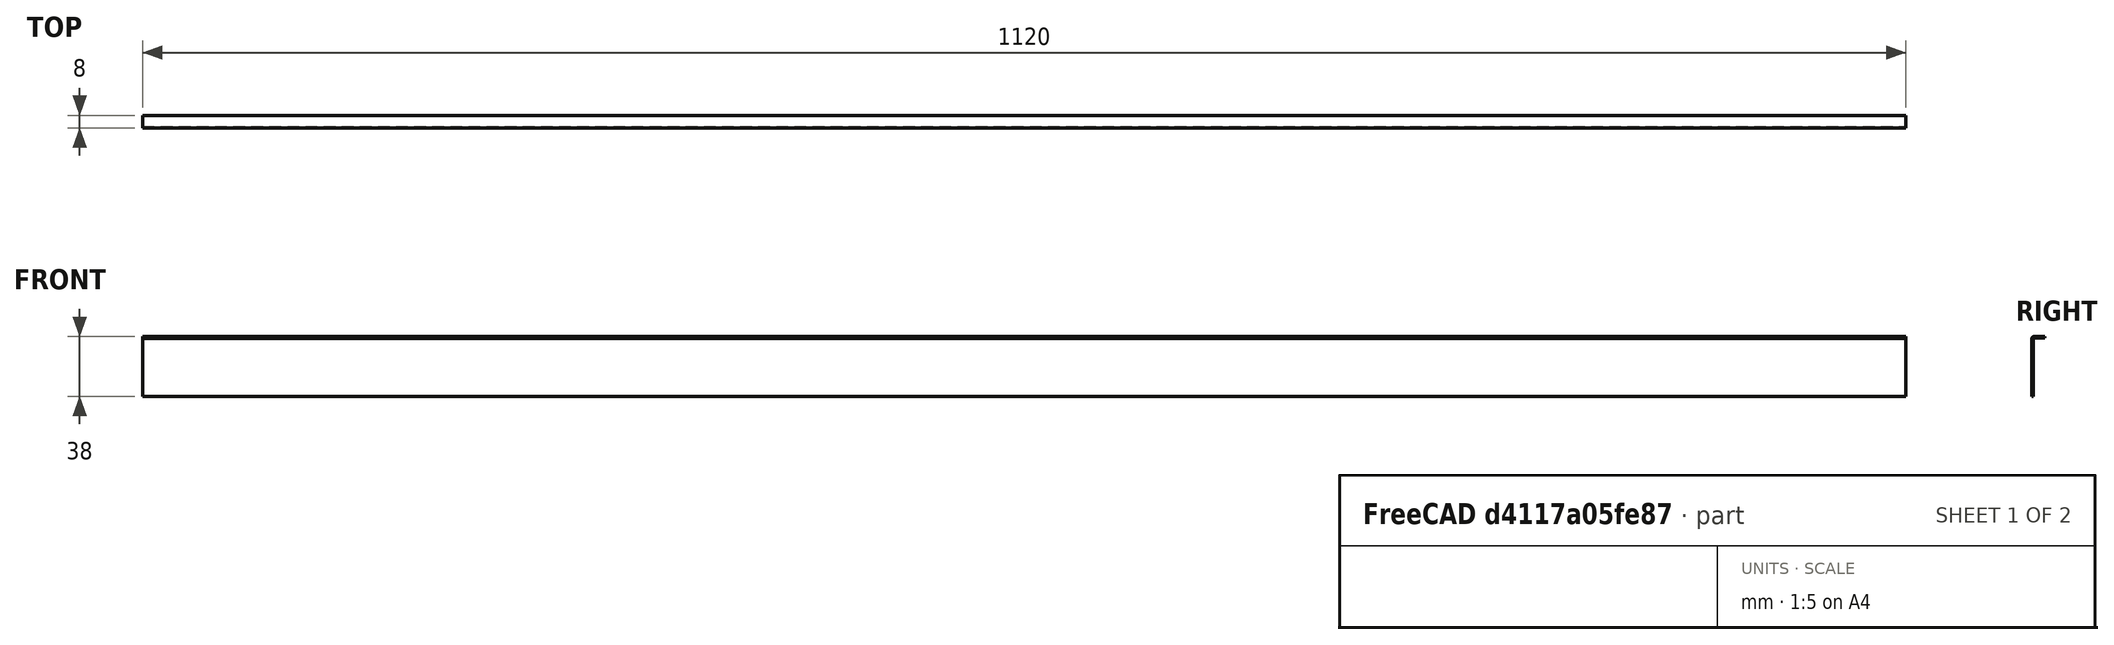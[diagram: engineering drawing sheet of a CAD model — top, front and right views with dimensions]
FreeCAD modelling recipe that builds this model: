
FCSTD DOCUMENT  (FreeCAD 0.16R6712 (Git))
Label: BandeauAluClavier
License: All rights reserved
LicenseURL: http://en.wikipedia.org/wiki/All_rights_reserved
objects: Drawing::FeatureViewPython×3, Part::Box×1, Part::FeaturePython×1, Drawing::FeatureViewPart×1, Drawing::FeaturePage×1
note: 2 computed .brp shape members not serialized (recipe doc carries the construction recipe); baked Part::Feature solids carry a one-line shape summary decoded from their .brp

FEATURE [Part::Box] Box  label="Cube"
  Height = 36.9
  Length = 1120
  Width = 1
FEATURE [Part::FeaturePython] Bend  # WARN: FeaturePython — macro-defined, semantics opaque (R4)
  angle = 90
  baseObject = -> Box [Face6]
  gap1 = 0
  gap2 = 0
  invert = false
  length = 6.9
  radius = 0.1
  reliefd = 1
  reliefw = 0.5
FEATURE [Drawing::FeatureViewPart] Ortho  label="Ortho_0_0"
  Direction = (1,0,0)
  HiddenWidth = 0.15
  LineWidth = 0.35
  Rotation = 0
  Scale = 5
  ShowHiddenLines = false
  ShowSmoothLines = false
  Source = -> Bend
  Tolerance = 0.05
  ViewResult = <g id="Ortho_0_0"\n   transform="rotate(0,53.5,66) translate(53.5,66) scale(5,5)"\n  >\n<g   stroke="rgb(0, 0, 0)"\n   stroke-width="0.07"\n   stroke-linecap="butt"\n   stroke-linejoin="miter"\n   fill="none"\n   transform="scale(1,-1)"\n  >\n<path id= "1" d=" M 38 -8 L 37 -8 " />\n<path id= "2" d=" M 37 -1.1 L 37 -8 " />\n<path id= "3" d=" M 38 -1.1 L 37 -1.1 " />\n<path id= "4" d=" M 38 -1.1 L 38 -8 " />\n<path d="M36.9 -1 A0.1 0.1 0 0 0 37 -1.1" /><path id= "6" d=" M 36.9 0 L 36.9 -1 " />\n<path d="M36.9 0 A1.1 1.1 0 0 0 38 -1.1" /><path id= "8" d=" M 0 -1 L 36.9 -1 " />\n<path id= "9" d=" M 0 0 L 36.9 0 " />\n<path id= "10" d=" M 0 0 L 0 -1 " />\n</g>\n</g>
  Visible = true
  X = 53.5
  Y = 66
FEATURE [Drawing::FeatureViewPython] dim001  # drawing view (typed FeaturePython)
  Rotation = 0
  ViewResult = <g> \n  <line x1="51.500000" y1="66.000000" x2="39.000000" y2="66.000000" style="stroke:rgb(0,0,255);stroke-width:0.30" />\n<line x1="51.500000" y1="71.000000" x2="39.000000" y2="71.000000" style="stroke:rgb(0,0,255);stroke-width:0.30" />\n<line x1="40.000000" y1="66.000000" x2="40.000000" y2="71.000000" style="stroke:rgb(0,0,255);stroke-width:0.30" /> \n  <polygon points="40.000000,71.000000 39.000000,74.000000 40.000000,75.000000 41.000000,74.000000" style="fill:rgb(0,0,255);stroke:rgb(0,0,255);stroke-width:0" /><polygon points="40.000000,66.000000 41.000000,63.000000 40.000000,62.000000 39.000000,63.000000" style="fill:rgb(0,0,255);stroke:rgb(0,0,255);stroke-width:0" /> \n  <text x="38.000000" y="68.500000" font-family="Verdana" font-size="3.6" fill="rgb(0,0,255)" text-anchor="middle" transform="rotate(-90.000000 38.000000,68.500000)" >  1</text> </g>
  Visible = true
  X = 0
  Y = 0
  arrowL1 = 3
  arrowL2 = 1
  arrowW = 2
  arrow_scheme = 0
  autoPlaceOffset = 2
  autoPlaceText = true
  click1_x = 40
  click1_y = 70
  click2_x = 40
  click2_y = 70
  comma_decimal_place = false
  dimension_line_overshoot = 1
  gap_datum_points = 2
  halfDimension_linear = false
  lineColor = rgb(0,0,255)
  strokeWidth = 0.3
  textFormat_linear = %(value)3.0f
  textRenderer_color = rgb(0,0,255)
  textRenderer_family = Verdana
  textRenderer_size = 3.6
  unit_custom_scale = 1
  unit_scheme = 0
FEATURE [Drawing::FeatureViewPython] dim002  # drawing view (typed FeaturePython)
  Rotation = 0
  ViewResult = <g> \n  <line x1="53.500000" y1="64.000000" x2="53.500000" y2="39.000000" style="stroke:rgb(0,0,255);stroke-width:0.30" />\n<line x1="243.500000" y1="69.500000" x2="243.500000" y2="39.000000" style="stroke:rgb(0,0,255);stroke-width:0.30" />\n<line x1="53.500000" y1="40.000000" x2="243.500000" y2="40.000000" style="stroke:rgb(0,0,255);stroke-width:0.30" /> \n  <polygon points="243.500000,40.000000 240.500000,39.000000 239.500000,40.000000 240.500000,41.000000" style="fill:rgb(0,0,255);stroke:rgb(0,0,255);stroke-width:0" /><polygon points="53.500000,40.000000 56.500000,41.000000 57.500000,40.000000 56.500000,39.000000" style="fill:rgb(0,0,255);stroke:rgb(0,0,255);stroke-width:0" /> \n  <text x="148.500000" y="38.000000" font-family="Verdana" font-size="3.6" fill="rgb(0,0,255)" text-anchor="middle" transform="rotate(0.000000 148.500000,38.000000)" > 38</text> </g>
  Visible = true
  X = 0
  Y = 0
  arrowL1 = 3
  arrowL2 = 1
  arrowW = 2
  arrow_scheme = 0
  autoPlaceOffset = 2
  autoPlaceText = true
  click1_x = 240
  click1_y = 40
  click2_x = 240
  click2_y = 40
  comma_decimal_place = false
  dimension_line_overshoot = 1
  gap_datum_points = 2
  halfDimension_linear = false
  lineColor = rgb(0,0,255)
  strokeWidth = 0.3
  textFormat_linear = %(value)3.0f
  textRenderer_color = rgb(0,0,255)
  textRenderer_family = Verdana
  textRenderer_size = 3.6
  unit_custom_scale = 1
  unit_scheme = 0
FEATURE [Drawing::FeatureViewPython] dim003  # drawing view (typed FeaturePython)
  Rotation = 0
  ViewResult = <g> \n  <line x1="245.500000" y1="106.000000" x2="271.000000" y2="106.000000" style="stroke:rgb(0,0,255);stroke-width:0.30" />\n<line x1="240.000000" y1="66.000000" x2="271.000000" y2="66.000000" style="stroke:rgb(0,0,255);stroke-width:0.30" />\n<line x1="270.000000" y1="106.000000" x2="270.000000" y2="66.000000" style="stroke:rgb(0,0,255);stroke-width:0.30" /> \n  <polygon points="270.000000,66.000000 269.000000,69.000000 270.000000,70.000000 271.000000,69.000000" style="fill:rgb(0,0,255);stroke:rgb(0,0,255);stroke-width:0" /><polygon points="270.000000,106.000000 271.000000,103.000000 270.000000,102.000000 269.000000,103.000000" style="fill:rgb(0,0,255);stroke:rgb(0,0,255);stroke-width:0" /> \n  <text x="268.000000" y="86.000000" font-family="Verdana" font-size="3.6" fill="rgb(0,0,255)" text-anchor="middle" transform="rotate(-90.000000 268.000000,86.000000)" >  8</text> </g>
  Visible = true
  X = 0
  Y = 0
  arrowL1 = 3
  arrowL2 = 1
  arrowW = 2
  arrow_scheme = 0
  autoPlaceOffset = 2
  autoPlaceText = true
  click1_x = 270
  click1_y = 75
  click2_x = 270
  click2_y = 75
  comma_decimal_place = false
  dimension_line_overshoot = 1
  gap_datum_points = 2
  halfDimension_linear = false
  lineColor = rgb(0,0,255)
  strokeWidth = 0.3
  textFormat_linear = %(value)3.0f
  textRenderer_color = rgb(0,0,255)
  textRenderer_family = Verdana
  textRenderer_size = 3.6
  unit_custom_scale = 1
  unit_scheme = 0
FEATURE [Drawing::FeaturePage] Page
  EditableTexts = GB | Console Orgue | Bandeau clavier (acier long. 1120mm) | 2 exemplaires | A4 | X / Y | 5 | PN | DN | DD/MM/YYYY | REV A
  Group = -> [Ortho,dim001,dim002,dim003]
